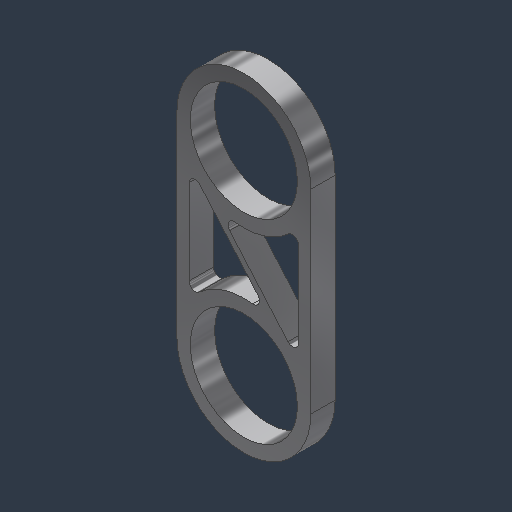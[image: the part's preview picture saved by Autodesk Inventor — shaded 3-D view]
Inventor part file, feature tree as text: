
AUTODESK INVENTOR PART (.ipt)
format: ipt  version: 2024.3 (Build 283343000, 343)  size: 147,968 bytes
history: native  units: mm (DEFAULTED — no unit token found)
features: sketch x2, extrude x1, hole x1, fillet x1
ambient origin geometry x8: Origin, YZ Plane, XZ Plane, XY Plane, X Axis, Y Axis, Z Axis, Center Point
bodies: Solid1 (feature_tree)
feature tree (5):
  extrude  "Extrusion1"  Depth=28.575mm
  hole  "Hole1"  [1 undecoded]
  fillet  "Fillet1"  Radius=1.5875mm
  sketch  "Sketch2"  dims[d3=28.575mm d4=50.8mm]
  sketch  "Sketch3"  dims[d5=19.05mm d6=6.35mm d7=0.0mm d8=27.94mm d9=10.0mm d10=9.525mm d11=6.35mm d12=14.3117mm d13=15.0mm d14=20.594885mm d15=1.5875mm d16=17.4625mm d17=1.5875mm d18=3.175mm]
note: 1 required parameter value undecoded (feature->parameter linkage not recoverable at this tier; creation-order binding heuristic only, values carry confidence <= 0.55)
